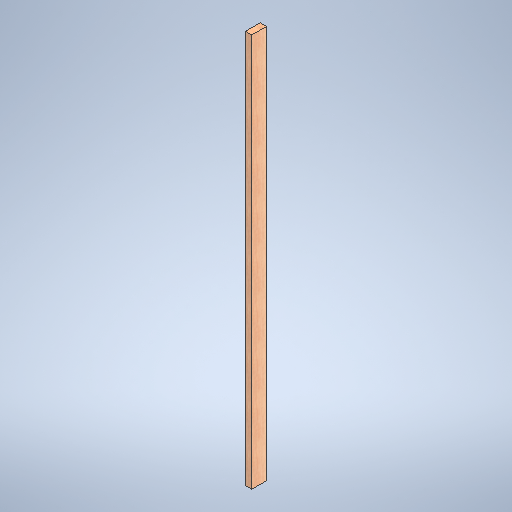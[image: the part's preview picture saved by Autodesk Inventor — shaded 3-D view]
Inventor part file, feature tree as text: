
AUTODESK INVENTOR PART (.ipt)
format: ipt  version: 2025 (Build 290162010, 162A)  size: 278,016 bytes
history: native  units: in
note: dims shown in document units (in); Inventor stores cm internally (conversion verified against a paired STEP export)
features: extrude x1, sketch x1
ambient origin geometry x8: Origin, YZ Plane, XZ Plane, XY Plane, X Axis, Y Axis, Z Axis, Center Point
bodies: Solid1 (feature_tree)
feature tree (2):
  extrude  "Extrusion1"  Depth=1.5in
  sketch  "Sketch1"  dims[d0=3.5in d1=1.5in d2=93.0in d3=0.0in]
